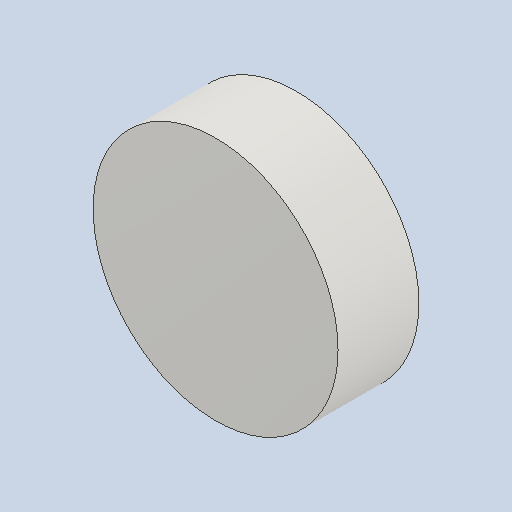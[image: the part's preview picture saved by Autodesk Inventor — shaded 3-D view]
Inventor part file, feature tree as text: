
AUTODESK INVENTOR PART (.ipt)
format: ipt  version: 2024 (Build 280153000, 153)  size: 82,432 bytes
history: native  units: mm (DEFAULTED — no unit token found)
features: extrude x1, other x1
ambient origin geometry x8: Origin, YZ Plane, XZ Plane, XY Plane, X Axis, Y Axis, Z Axis, Center Point
bodies: Solid1 (feature_tree)
feature tree (2):
  extrude  "Pulley"  Depth=20.0mm
  other  "Main Sketch"
